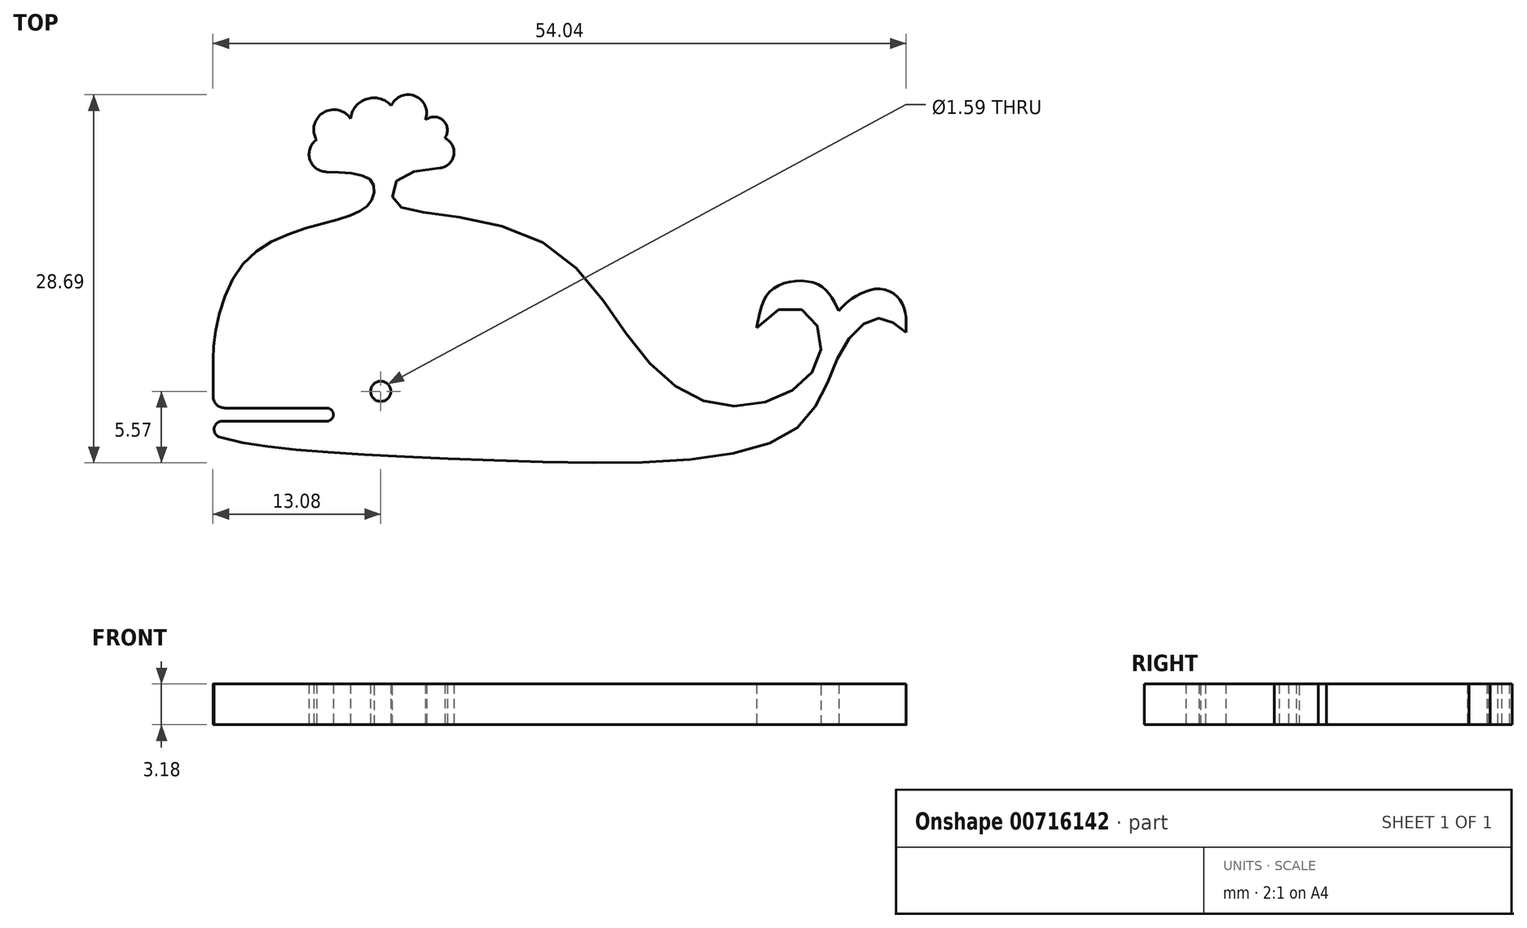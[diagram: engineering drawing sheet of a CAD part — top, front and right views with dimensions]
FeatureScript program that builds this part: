
annotation { "Feature Type Name" : "Feature", "Feature Type Description" : "" }
export const myFeature = defineFeature(function(context is Context, id is Id, definition is map)
    precondition{}
    {
        {
            var Q0;
            Q0=qCreatedBy(makeId("Top.planeOp"),FACE);
            var sketch = newSketch(context, id + "F0", { "sketchPlane" : qUnion([Q0])});
            skCircle(sketch, "E0", {"center": v(0, 0) * mm, "radius": 0.8 * mm});
            skLineSegment(sketch, "E1", {"start": v(-4.21, -1.3) * mm, "end": v(-12.15, -1.3) * mm});
            skLineSegment(sketch, "E2", {"start": v(-4.21, -2.33) * mm, "end": v(-12.36, -2.33) * mm});
            skArc(sketch, "E3", {"start": v(-4.21, -2.33) * mm, "mid": v(-3.7, -1.82) * mm, "end": v(-4.21, -1.3) * mm});
            skFitSpline(sketch, "E4", {"points": [v(-12.54, -3.57) * mm, v(-5.3, -4.64) * mm, v(13.4, -5.52) * mm, v(32.32, -2.95) * mm, v(35.94, 3.23) * mm, v(38.78, 5.69) * mm, v(40.95, 4.58) * mm], "startDerivative": vector(39.97, -12) * mm, "endDerivative": vector(23.64, -19.5) * mm});
            skArc(sketch, "E5", {"start": v(-12.36, -2.33) * mm, "mid": v(-12.99, -2.87) * mm, "end": v(-12.54, -3.57) * mm});
            skArc(sketch, "E6", {"start": v(-13.08, -0.37) * mm, "mid": v(-12.8, -1.03) * mm, "end": v(-12.15, -1.3) * mm});
            skLineSegment(sketch, "E7", {"start": v(-13.08, -0.37) * mm, "end": v(-13.08, 2.5) * mm});
            skFitSpline(sketch, "E8", {"points": [v(-13.08, 2.5) * mm, v(-10.4, 10.3) * mm, v(-2.57, 13.63) * mm, v(-0.66, 15.01) * mm, v(-0.78, 16.45) * mm, v(-4.25, 17.1) * mm], "startDerivative": vector(0, 20.45) * mm, "endDerivative": vector(-22.74, 0.59) * mm});
            skFitSpline(sketch, "E9", {"points": [v(4.62, 17.4) * mm, v(1.26, 16.45) * mm, v(1.02, 14.83) * mm, v(2.7, 14.05) * mm, v(12.96, 11.41) * mm, v(20.2, 3.1) * mm, v(26, -0.98) * mm, v(31.93, 0) * mm, v(34.33, 3.33) * mm, v(32.9, 6.33) * mm, v(29.3, 4.95) * mm], "startDerivative": vector(-49.37, -5.24) * mm, "endDerivative": vector(-32.59, -48.88) * mm});
            skArc(sketch, "E10", {"start": v(-5, 19.6) * mm, "mid": v(-5.53, 18.08) * mm, "end": v(-4.25, 17.1) * mm});
            skArc(sketch, "E11", {"start": v(4.62, 17.4) * mm, "mid": v(5.7, 18.43) * mm, "end": v(5, 19.75) * mm});
            skArc(sketch, "E12", {"start": v(-2.36, 21.26) * mm, "mid": v(-4.49, 21.72) * mm, "end": v(-5, 19.6) * mm});
            skArc(sketch, "E13", {"start": v(0.81, 22.27) * mm, "mid": v(-1.1, 22.79) * mm, "end": v(-2.36, 21.26) * mm});
            skArc(sketch, "E14", {"start": v(3.48, 21.15) * mm, "mid": v(2.7, 23) * mm, "end": v(0.81, 22.27) * mm});
            skArc(sketch, "E15", {"start": v(5, 19.75) * mm, "mid": v(4.86, 21.12) * mm, "end": v(3.48, 21.15) * mm});
            skFitSpline(sketch, "E16", {"points": [v(29.3, 4.95) * mm, v(30.59, 8) * mm, v(34.06, 8.34) * mm, v(35.7, 6.27) * mm], "startDerivative": vector(1.82, 10.47) * mm, "endDerivative": vector(3.85, -8.2) * mm});
            skFitSpline(sketch, "E17", {"points": [v(40.95, 4.58) * mm, v(40.62, 6.9) * mm, v(38.88, 7.99) * mm, v(36.62, 7.14) * mm, v(35.7, 6.27) * mm], "startDerivative": vector(0.13, 9.2) * mm, "endDerivative": vector(-3.77, -4.29) * mm});
            skLineSegment(sketch, "E18.bottom", {"start": v(-15.25, 24.06) * mm, "end": v(43.2, 24.06) * mm, "construction": true});
            skLineSegment(sketch, "E18.top", {"start": v(-15.25, -9.53) * mm, "end": v(43.2, -9.53) * mm, "construction": true});
            skLineSegment(sketch, "E18.left", {"start": v(-15.25, 24.06) * mm, "end": v(-15.25, -9.53) * mm, "construction": true});
            skLineSegment(sketch, "E18.right", {"start": v(43.2, 24.06) * mm, "end": v(43.2, -9.53) * mm, "construction": true});
            skPoint(sketch, "E18.middle", {"position": v(13.98, 7.27) * mm});
            skSolve(sketch);
        }
        {
            var Q0;
            Q0 = qSketchRegion(id + "F0", true);
            extrude(context, id + "F1", {"entities" : qUnion([Q0]), "depth" : 3.17 * mm, "offsetDistance" : 25.4 * mm});
        }
    });
